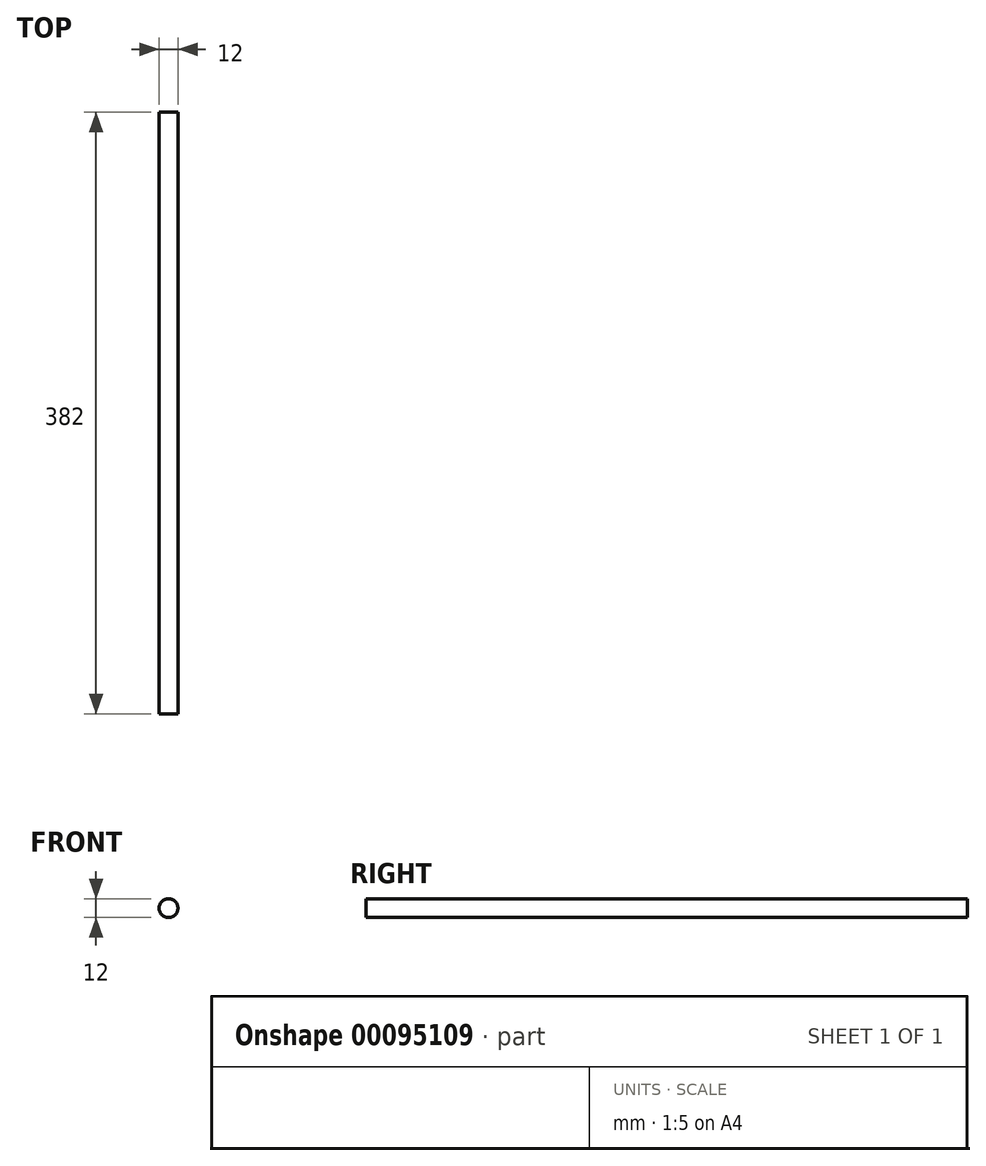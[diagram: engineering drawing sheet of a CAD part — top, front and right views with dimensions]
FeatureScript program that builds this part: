
annotation { "Feature Type Name" : "Feature", "Feature Type Description" : "" }
export const myFeature = defineFeature(function(context is Context, id is Id, definition is map)
    precondition{}
    {
        {
            var Q0;
            Q0=qCreatedBy(makeId("Front.planeOp"),FACE);
            var sketch = newSketch(context, id + "F0", { "sketchPlane" : qUnion([Q0])});
            skCircle(sketch, "E0", {"center": v(0, 0) * mm, "radius": 6 * mm});
            skSolve(sketch);
        }
        {
            var Q0;
            Q0=makeQuery(id+"F0.imprint","IMPRINT",FACE,{"disambiguationData":[TD([[makeQuery(id+"F0.imprint","IMPRINT",EDGE,{"derivedFrom":sQuery(id+"F0.wireOp",EDGE,"E0")}),1.0]])]});
            extrude(context, id + "F1", {"entities" : qUnion([Q0]), "oppositeDirection" : true, "depth" : 382 * mm});
        }
    });
